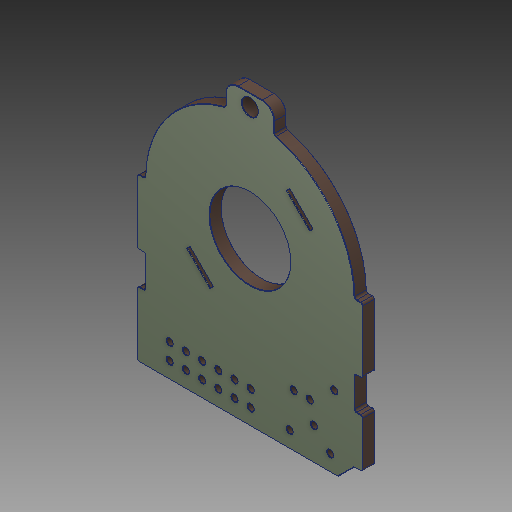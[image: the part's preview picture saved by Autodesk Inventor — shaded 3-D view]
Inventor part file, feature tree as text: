
AUTODESK INVENTOR PART (.ipt)
format: ipt  version: 2019 (Build 230136000, 136)  size: 279,040 bytes
history: mixed  units: mm
features: other x1, fillet x1, imported_body x1
ambient origin geometry x8: Origin, YZ Plane, XZ Plane, XY Plane, X Axis, Y Axis, Z Axis, Center Point
bodies: Body1 (imported_parasolid)
feature tree (3):
  other  "Твердое тело1"
  fillet  "Fillet1"  [1 undecoded]
  imported_body  NMx_Import_Brep_tag  [imported B-rep: ~179 faces, bbox_mm=[27.8, 35.546314, 1.5]]
note: 1 required parameter value undecoded (feature->parameter linkage not recoverable at this tier; creation-order binding heuristic only, values carry confidence <= 0.55)
